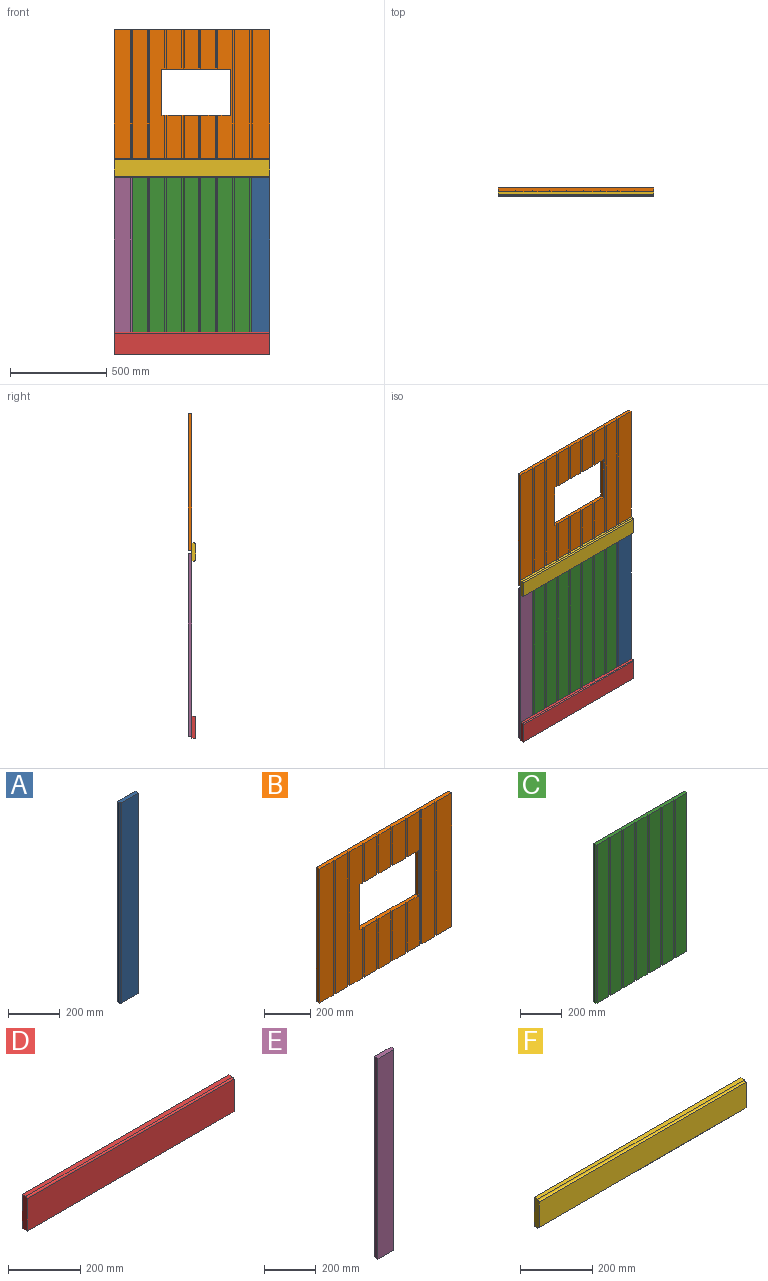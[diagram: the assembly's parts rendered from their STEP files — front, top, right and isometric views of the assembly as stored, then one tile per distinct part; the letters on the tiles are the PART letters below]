
ASSEMBLY  parts=6 mates=5
PART A: 7 faces, bbox 100x19x950 mm
  f0: plane 100x19mm, normal (0,0,1), area 1882mm2, adj f1,f3,f4,f5,f6
  f1: plane 950x13mm, normal (-1,0,0), area 12350mm2, adj f0,f2,f4,f6
  f2: plane 100x19mm, normal (0,0,-1), area 1882mm2, adj f1,f3,f4,f5,f6
  f3: plane 950x19mm, normal (1,0,0), area 18050mm2, adj f0,f2,f4,f5
  f4: plane 950x100mm, normal (0,1,0), area 95000mm2, adj f0,f1,f2,f3
  f5: plane 950x94mm, normal (0,-1,0), area 89300mm2, adj f0,f2,f3,f6
  f6: plane 950x6mm, normal (-0.71,-0.71,0), area 8061mm2, adj f0,f1,f2,f5
PART B: 57 faces, bbox 810x19x710 mm
  f0: plane 710x76mm, normal (0,-1,0), area 53960mm2, adj f12,f15,f54,f55
  f1: plane 710x93mm, normal (0,-1,0), area 66030mm2, adj f12,f15,f17,f41
  f2: plane 710x76mm, normal (0,-1,0), area 53960mm2, adj f12,f15,f42,f43
  f3: plane 710x76mm, normal (0,-1,0), area 38120mm2, adj f11,f12,f14,f15,f18,f33,f44,f45
  f4: plane 710x76mm, normal (0,-1,0), area 50600mm2, adj f11,f12,f13,f15,f18,f40,f52,f53
  f5: plane 205x76mm, normal (0,-1,0), area 15580mm2, adj f11,f15,f50,f51
  f6: plane 205x73mm, normal (0,-1,0), area 14965mm2, adj f11,f15,f48,f49
  f7: plane 205x76mm, normal (0,-1,0), area 15580mm2, adj f11,f15,f46,f47
  f8: plane 265x76mm, normal (0,-1,0), area 20140mm2, adj f12,f18,f34,f35
  f9: plane 265x73mm, normal (0,-1,0), area 19345mm2, adj f12,f18,f36,f37
  f10: plane 265x76mm, normal (0,-1,0), area 20140mm2, adj f12,f18,f38,f39
  f11: plane 357x19mm, normal (0,0,-1), area 6615mm2, adj f3,f4,f5,f6,f7,f13,f14,f19
  f12: plane 810x19mm, normal (0,0,-1), area 15054mm2, adj f0,f1,f2,f3,f4,f8,f9,f10
  f13: plane 240x19mm, normal (1,0,0), area 4560mm2, adj f4,f11,f18,f19
  f14: plane 240x19mm, normal (-1,0,0), area 4560mm2, adj f3,f11,f18,f19
  f15: plane 810x19mm, normal (0,0,1), area 15054mm2, adj f0,f1,f2,f3,f4,f5,f6,f7
  f16: plane 710x19mm, normal (-1,0,0), area 13490mm2, adj f12,f15,f19,f20
  f17: plane 710x19mm, normal (1,0,0), area 13490mm2, adj f1,f12,f15,f19
  f18: plane 357x19mm, normal (0,0,1), area 6615mm2, adj f3,f4,f8,f9,f10,f13,f14,f19
  f19: plane 810x710mm, normal (0,1,0), area 489420mm2, adj f11,f12,f13,f14,f15,f16,f17,f18
  f20: plane 710x84mm, normal (0,-1,0), area 59640mm2, adj f12,f15,f16,f56
  f21: plane 265x1mm, normal (0,-1,0), area 265mm2, adj f12,f18,f39,f40
  f22: plane 265x1mm, normal (0,-1,0), area 265mm2, adj f12,f18,f37,f38
  f23: plane 265x1mm, normal (0,-1,0), area 265mm2, adj f12,f18,f35,f36
  f24: plane 265x1mm, normal (0,-1,0), area 265mm2, adj f12,f18,f33,f34
  f25: plane 710x1mm, normal (0,-1,0), area 710mm2, adj f12,f15,f53,f54
  f26: plane 710x1mm, normal (0,-1,0), area 710mm2, adj f12,f15,f43,f44
  f27: plane 710x1mm, normal (0,-1,0), area 710mm2, adj f12,f15,f41,f42
  f28: plane 710x1mm, normal (0,-1,0), area 710mm2, adj f12,f15,f55,f56
  f29: plane 205x1mm, normal (0,-1,0), area 205mm2, adj f11,f15,f45,f46
  f30: plane 205x1mm, normal (0,-1,0), area 205mm2, adj f11,f15,f47,f48
  f31: plane 205x1mm, normal (0,-1,0), area 205mm2, adj f11,f15,f49,f50
  f32: plane 205x1mm, normal (0,-1,0), area 205mm2, adj f11,f15,f51,f52
  f33: plane 265x6mm, normal (-0.71,-0.71,0), area 2248.6mm2, adj f3,f12,f18,f24
  f34: plane 265x6mm, normal (0.71,-0.71,0), area 2248.6mm2, adj f8,f12,f18,f24
  f35: plane 265x6mm, normal (-0.71,-0.71,0), area 2248.6mm2, adj f8,f12,f18,f23
  f36: plane 265x6mm, normal (0.71,-0.71,0), area 2248.6mm2, adj f9,f12,f18,f23
  f37: plane 265x6mm, normal (-0.71,-0.71,0), area 2248.6mm2, adj f9,f12,f18,f22
  f38: plane 265x6mm, normal (0.71,-0.71,0), area 2248.6mm2, adj f10,f12,f18,f22
  f39: plane 265x6mm, normal (-0.71,-0.71,0), area 2248.6mm2, adj f10,f12,f18,f21
  f40: plane 265x6mm, normal (0.71,-0.71,0), area 2248.6mm2, adj f4,f12,f18,f21
  f41: plane 710x6mm, normal (-0.71,-0.71,0), area 6024.5mm2, adj f1,f12,f15,f27
  f42: plane 710x6mm, normal (0.71,-0.71,0), area 6024.5mm2, adj f2,f12,f15,f27
  f43: plane 710x6mm, normal (-0.71,-0.71,0), area 6024.5mm2, adj f2,f12,f15,f26
  f44: plane 710x6mm, normal (0.71,-0.71,0), area 6024.5mm2, adj f3,f12,f15,f26
  f45: plane 205x6mm, normal (-0.71,-0.71,0), area 1739.5mm2, adj f3,f11,f15,f29
  f46: plane 205x6mm, normal (0.71,-0.71,0), area 1739.5mm2, adj f7,f11,f15,f29
  f47: plane 205x6mm, normal (-0.71,-0.71,0), area 1739.5mm2, adj f7,f11,f15,f30
  f48: plane 205x6mm, normal (0.71,-0.71,0), area 1739.5mm2, adj f6,f11,f15,f30
  f49: plane 205x6mm, normal (-0.71,-0.71,0), area 1739.5mm2, adj f6,f11,f15,f31
  f50: plane 205x6mm, normal (0.71,-0.71,0), area 1739.5mm2, adj f5,f11,f15,f31
  f51: plane 205x6mm, normal (-0.71,-0.71,0), area 1739.5mm2, adj f5,f11,f15,f32
  f52: plane 205x6mm, normal (0.71,-0.71,0), area 1739.5mm2, adj f4,f11,f15,f32
  f53: plane 710x6mm, normal (-0.71,-0.71,0), area 6024.5mm2, adj f4,f12,f15,f25
  f54: plane 710x6mm, normal (0.71,-0.71,0), area 6024.5mm2, adj f0,f12,f15,f25
  f55: plane 710x6mm, normal (-0.71,-0.71,0), area 6024.5mm2, adj f0,f12,f15,f28
  f56: plane 710x6mm, normal (0.71,-0.71,0), area 6024.5mm2, adj f12,f15,f20,f28
PART C: 32 faces, bbox 619x19x930 mm
  f0: plane 930x76mm, normal (0,-1,0), area 70680mm2, adj f6,f7,f21,f30
  f1: plane 930x76mm, normal (0,-1,0), area 70680mm2, adj f6,f7,f22,f29
  f2: plane 930x73mm, normal (0,-1,0), area 67890mm2, adj f6,f7,f23,f28
  f3: plane 930x76mm, normal (0,-1,0), area 70680mm2, adj f6,f7,f24,f27
  f4: plane 930x76mm, normal (0,-1,0), area 70680mm2, adj f6,f7,f19,f26
  f5: plane 930x76mm, normal (0,-1,0), area 70680mm2, adj f6,f7,f18,f25
  f6: plane 619x19mm, normal (0,0,-1), area 11473mm2, adj f0,f1,f2,f3,f4,f5,f8,f9
  f7: plane 619x19mm, normal (0,0,1), area 11473mm2, adj f0,f1,f2,f3,f4,f5,f8,f9
  f8: plane 930x13mm, normal (-1,0,0), area 12090mm2, adj f6,f7,f10,f31
  f9: plane 930x13mm, normal (1,0,0), area 12090mm2, adj f6,f7,f10,f25
  f10: plane 930x619mm, normal (0,1,0), area 575670mm2, adj f6,f7,f8,f9
  f11: plane 930x76mm, normal (0,-1,0), area 70680mm2, adj f6,f7,f20,f31
  f12: plane 930x1mm, normal (0,-1,0), area 930mm2, adj f6,f7,f18,f19
  f13: plane 930x1mm, normal (0,-1,0), area 930mm2, adj f6,f7,f24,f26
  f14: plane 930x1mm, normal (0,-1,0), area 930mm2, adj f6,f7,f23,f27
  f15: plane 930x1mm, normal (0,-1,0), area 930mm2, adj f6,f7,f22,f28
  f16: plane 930x1mm, normal (0,-1,0), area 930mm2, adj f6,f7,f21,f29
  f17: plane 930x1mm, normal (0,-1,0), area 930mm2, adj f6,f7,f20,f30
  f18: plane 930x6mm, normal (-0.71,-0.71,0), area 7891.3mm2, adj f5,f6,f7,f12
  f19: plane 930x6mm, normal (0.71,-0.71,0), area 7891.3mm2, adj f4,f6,f7,f12
  f20: plane 930x6mm, normal (0.71,-0.71,0), area 7891.3mm2, adj f6,f7,f11,f17
  f21: plane 930x6mm, normal (0.71,-0.71,0), area 7891.3mm2, adj f0,f6,f7,f16
  f22: plane 930x6mm, normal (0.71,-0.71,0), area 7891.3mm2, adj f1,f6,f7,f15
  f23: plane 930x6mm, normal (0.71,-0.71,0), area 7891.3mm2, adj f2,f6,f7,f14
  f24: plane 930x6mm, normal (0.71,-0.71,0), area 7891.3mm2, adj f3,f6,f7,f13
  f25: plane 930x6mm, normal (0.71,-0.71,0), area 7891.3mm2, adj f5,f6,f7,f9
  f26: plane 930x6mm, normal (-0.71,-0.71,0), area 7891.3mm2, adj f4,f6,f7,f13
  f27: plane 930x6mm, normal (-0.71,-0.71,0), area 7891.3mm2, adj f3,f6,f7,f14
  f28: plane 930x6mm, normal (-0.71,-0.71,0), area 7891.3mm2, adj f2,f6,f7,f15
  f29: plane 930x6mm, normal (-0.71,-0.71,0), area 7891.3mm2, adj f1,f6,f7,f16
  f30: plane 930x6mm, normal (-0.71,-0.71,0), area 7891.3mm2, adj f0,f6,f7,f17
  f31: plane 930x6mm, normal (-0.71,-0.71,0), area 7891.3mm2, adj f6,f7,f8,f11
PART D: 7 faces, bbox 810x20x115 mm
  f0: plane 810x15mm, normal (0,0,1), area 12150mm2, adj f1,f3,f4,f6
  f1: plane 115x20mm, normal (-1,0,0), area 2294.6mm2, adj f0,f2,f4,f5,f6
  f2: plane 810x20mm, normal (0,0,-1), area 16200mm2, adj f1,f3,f4,f5
  f3: plane 115x20mm, normal (1,0,0), area 2294.6mm2, adj f0,f2,f4,f5,f6
  f4: plane 810x115mm, normal (0,1,0), area 93150mm2, adj f0,f1,f2,f3
  f5: plane 810x110mm, normal (0,-1,0), area 89100mm2, adj f1,f2,f3,f6
  f6: cylinder r=5mm len=810mm, axis (-1,0,0), area 6361.7mm2, adj f0,f1,f3,f5
PART E: 7 faces, bbox 91x19x950 mm
  f0: plane 91x19mm, normal (0,0,1), area 1711mm2, adj f1,f3,f4,f5,f6
  f1: plane 950x19mm, normal (-1,0,0), area 18050mm2, adj f0,f2,f4,f5
  f2: plane 91x19mm, normal (0,0,-1), area 1711mm2, adj f1,f3,f4,f5,f6
  f3: plane 950x13mm, normal (1,0,0), area 12350mm2, adj f0,f2,f4,f6
  f4: plane 950x91mm, normal (0,1,0), area 86450mm2, adj f0,f1,f2,f3
  f5: plane 950x85mm, normal (0,-1,0), area 80750mm2, adj f0,f1,f2,f6
  f6: plane 950x6mm, normal (0.71,-0.71,0), area 8061mm2, adj f0,f2,f3,f5
PART F: 8 faces, bbox 810x20x98 mm
  f0: plane 98x20mm, normal (-1,0,0), area 1903.5mm2, adj f1,f2,f3,f5,f6,f7
  f1: plane 810x86mm, normal (0,-1,0), area 69660mm2, adj f0,f4,f6,f7
  f2: plane 810x14mm, normal (0,0,1), area 11340mm2, adj f0,f4,f5,f7
  f3: plane 810x14mm, normal (0,0,-1), area 11340mm2, adj f0,f4,f5,f6
  f4: plane 98x20mm, normal (1,0,0), area 1903.5mm2, adj f1,f2,f3,f5,f6,f7
  f5: plane 810x98mm, normal (0,1,0), area 79380mm2, adj f0,f2,f3,f4
  f6: cylinder r=6mm len=810mm, axis (-1,0,0), area 7634.1mm2, adj f0,f1,f3,f4
  f7: cylinder r=6mm len=810mm, axis (1,0,0), area 7634.1mm2, adj f0,f1,f2,f4
PLACE A t=(370.41,355.41,-304.31)mm
PLACE B t=(-9.56,355.41,668.37)mm
PLACE C t=(23.33,355.41,17.66)mm
PLACE D t=(0,335.41,21.09)mm
PLACE E t=(-337.66,355.41,-325.86)mm
PLACE F t=(-70.58,335.41,442.1)mm
MATE fastened E.f5 <-> D.f4  axis (0,-1,0) through (-410.48,355.41,-471.73)mm
MATE fastened F.f5 <-> E.f5  axis (0,1,0) through (-410.48,355.41,438.27)mm
MATE fastened A.f5 <-> D.f4  axis (0,-1,0) through (399.52,355.41,-471.73)mm
MATE fastened C.f11 <-> F.f5  axis (0,-1,0) through (-313.48,355.41,438.27)mm
MATE fastened B.f20 <-> F.f5  axis (0,-1,0) through (-410.48,355.41,536.27)mm
